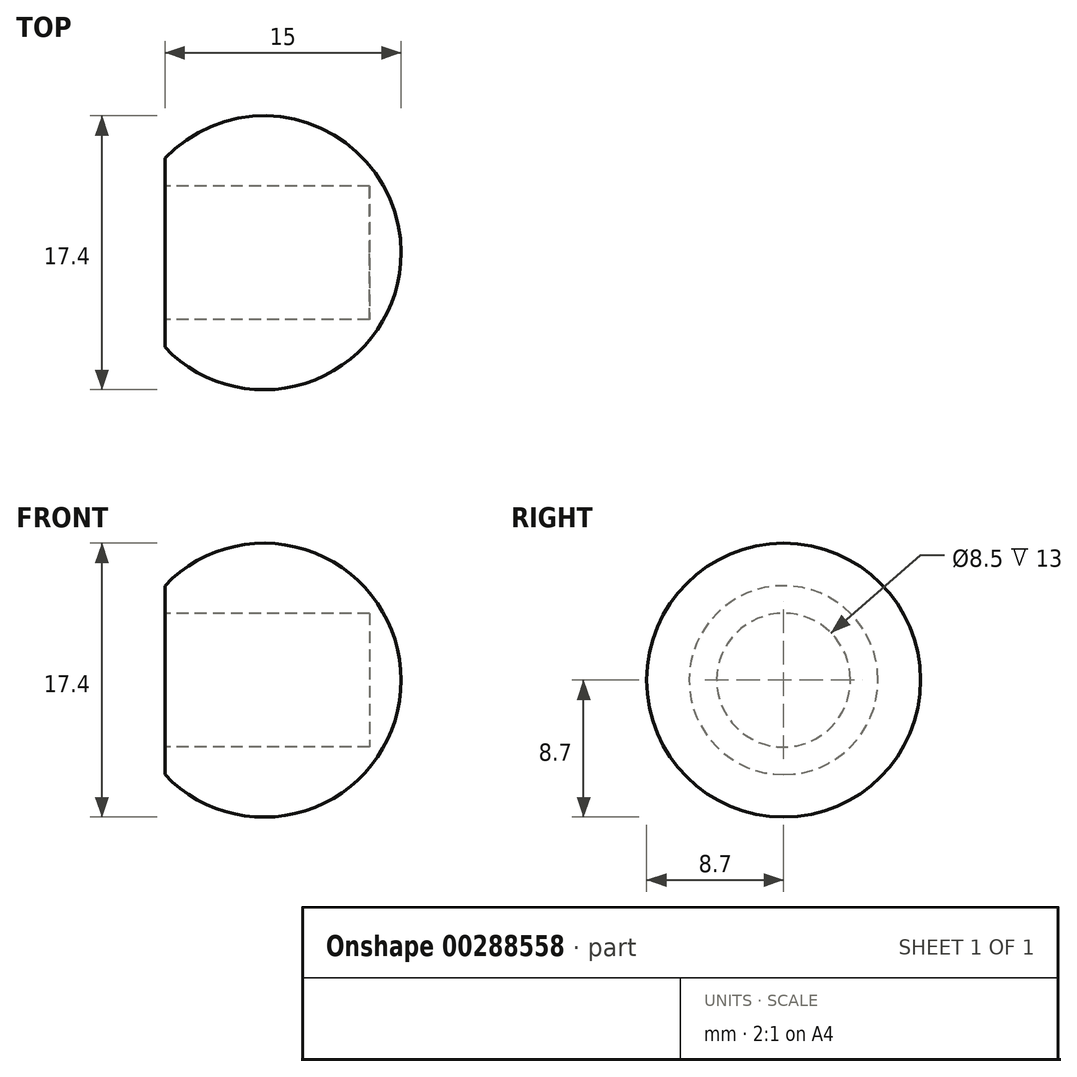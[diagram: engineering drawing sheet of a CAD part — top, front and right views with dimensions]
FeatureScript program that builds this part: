
annotation { "Feature Type Name" : "Feature", "Feature Type Description" : "" }
export const myFeature = defineFeature(function(context is Context, id is Id, definition is map)
    precondition{}
    {
        {
            var Q0;
            Q0=qCreatedBy(makeId("Top.planeOp"),FACE);
            var sketch = newSketch(context, id + "F0", { "sketchPlane" : qUnion([Q0])});
            skArc(sketch, "E0", {"start": v(0, -6) * mm, "mid": v(15, 0) * mm, "end": v(0, 6) * mm});
            skLineSegment(sketch, "E1", {"start": v(15, 0) * mm, "end": v(0, 0) * mm});
            skLineSegment(sketch, "E2", {"start": v(0, 0) * mm, "end": v(0, 6) * mm});
            skSolve(sketch);
        }
        {
            var Q0;
            {var subQ2=sQuery(id+"F0.wireOp",EDGE,"E1");Q0=makeQuery(id+"F0.imprint","IMPRINT",FACE,{"disambiguationData":[TD([[makeQuery(id+"F0.imprint","IMPRINT",EDGE,{"derivedFrom":subQ2}),-1.0]])]});}
            var Q1;
            Q1=sQuery(id+"F0.wireOp",EDGE,"E1");
            revolve(context, id + "F1", {"entities" : qUnion([Q0]), "axis" : qUnion([Q1]), "revolveType" : RevolveType.FULL});
        }
        {
            var Q0;
            Q0=makeQuery(id+"F1.opRevolve","SWEPT_FACE",FACE,{"disambiguationData":[OSD([sQuery(id+"F0.wireOp",EDGE,"E2")])]});
            var sketch = newSketch(context, id + "F2", { "sketchPlane" : qUnion([Q0])});
            skCircle(sketch, "E3", {"center": v(0, 0) * mm, "radius": 4.25 * mm});
            skSolve(sketch);
        }
        {
            var Q0;
            Q0=makeQuery(id+"F2.imprint","IMPRINT",FACE,{"disambiguationData":[TD([[makeQuery(id+"F2.imprint","IMPRINT",EDGE,{"derivedFrom":sQuery(id+"F2.wireOp",EDGE,"E3")}),1.0]])]});
            extrude(context, id + "F3", {"entities" : qUnion([Q0]), "operationType" : NewBodyOperationType.REMOVE, "oppositeDirection" : true, "depth" : 13 * mm});
        }
    });
